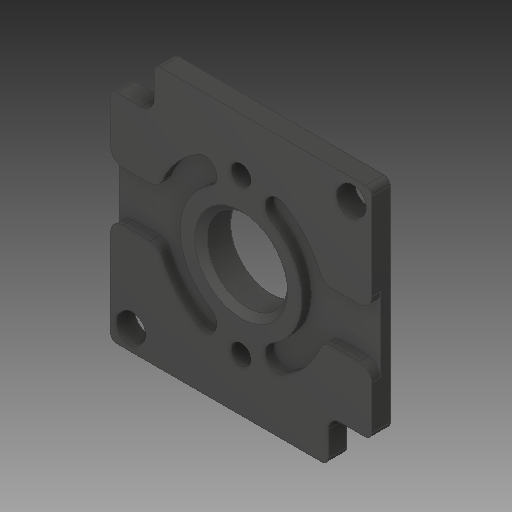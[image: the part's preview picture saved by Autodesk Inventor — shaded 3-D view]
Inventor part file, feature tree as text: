
AUTODESK INVENTOR PART (.ipt)
format: ipt  version: 2019 (Build 230136000, 136)  size: 265,728 bytes
history: native  units: in
note: dims shown in document units (in); Inventor stores cm internally (conversion verified against a paired STEP export)
features: fillet x1
ambient origin geometry x8: Origin, YZ Plane, XZ Plane, XY Plane, X Axis, Y Axis, Z Axis, Center Point
bodies: Solid1 (feature_tree)
feature tree (1):
  fillet  "Fillet4"  [1 undecoded]
note: 1 required parameter value undecoded (feature->parameter linkage not recoverable at this tier; creation-order binding heuristic only, values carry confidence <= 0.55)
